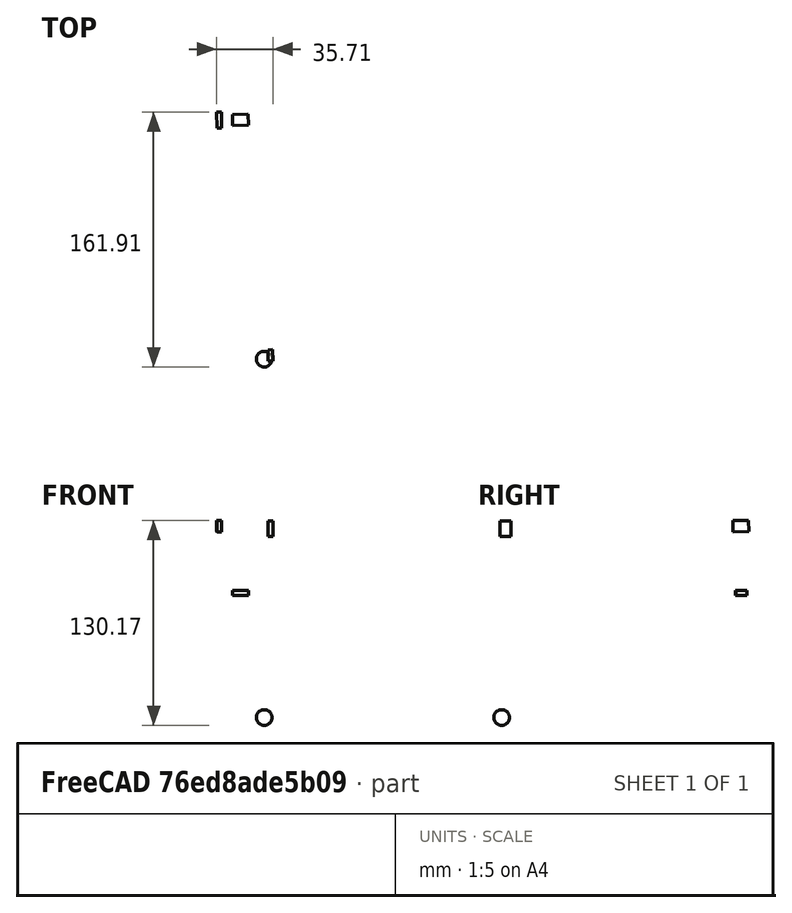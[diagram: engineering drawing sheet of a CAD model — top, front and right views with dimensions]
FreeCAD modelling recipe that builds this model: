
FCSTD DOCUMENT  (FreeCAD 2024.2R36189 (Git))
Label: 3axis_robot_forced_reduced
License: All rights reserved
LicenseURL: https://en.wikipedia.org/wiki/All_rights_reserved
objects: App::FeaturePython×9, App::Link×4, Part::FeaturePython×3, Part::Sphere×2, Assembly::JointGroup×1, Assembly::AssemblyObject×1
note: 5 computed .brp shape members not serialized (recipe doc carries the construction recipe); baked Part::Feature solids carry a one-line shape summary decoded from their .brp
EXTERNAL_REF file=base.FCStd obj=Part
EXTERNAL_REF file=arm0.FCStd obj=Part
EXTERNAL_REF file=arm1.FCStd obj=Part
EXTERNAL_REF file=arm2.FCStd obj=Part

FEATURE [App::Link] base  label="base 🔒"
  LinkedObject = -> <external base.FCStd>#Part
FEATURE [App::Link] arm0
  LinkPlacement = pos=(0,0,7) rot=(0,0,1;0.017159rad)
  LinkedObject = -> <external arm0.FCStd>#Part
  Placement = pos=(0,0,7) rot=(0,0,1;0.017159rad)
FEATURE [App::Link] arm1
  LinkPlacement = pos=(7.99882,0.137262,71) rot=(0.568594,0.584797,-0.578544;4.18519rad)
  LinkedObject = -> <external arm1.FCStd>#Part
  Placement = pos=(7.99882,0.137262,71) rot=(0.568594,0.584797,-0.578544;4.18519rad)
FEATURE [App::Link] arm2
  LinkPlacement = pos=(17.5713,-149.712,69.3598) rot=(0.707165,-0.000774,-0.707048;3.11578rad)
  LinkedObject = -> <external arm2.FCStd>#Part
  Placement = pos=(17.5713,-149.712,69.3598) rot=(0.707165,-0.000774,-0.707048;3.11578rad)
FEATURE [App::FeaturePython] GroundedJoint  # Assembly grounded joint (typed FeaturePython)
  ObjectToGround = -> base
FEATURE [App::FeaturePython] Revolute  # Assembly joint (typed FeaturePython)
  Activated = true
  Detach1 = false
  Detach2 = false
  Distance = 0
  Element1 = Edge30
  Element2 = Edge3
  JointType = 1 (Revolute)
  Object1 = Body
  Object2 = Body
  Offset = (0,0,-3)
  Part1 = -> base
  Part2 = -> arm0
  Placement1 = pos=(0,0,4) rot=(0,0,1;0rad)
  Placement2 = pos=(0,0,-3) rot=(0,0,1;0rad)
  Rotation = 0
  Vertex1 = Edge30
  Vertex2 = Edge3
FEATURE [App::FeaturePython] Revolute001  # Assembly joint (typed FeaturePython)
  Activated = true
  Detach1 = false
  Detach2 = false
  Distance = 0
  Element1 = Edge18
  Element2 = Edge23
  JointType = 1 (Revolute)
  Object1 = Body001
  Object2 = Body
  Offset = (0,0,-3)
  Part1 = -> arm1
  Part2 = -> arm0
  Placement2 = pos=(8,5.2e-15,64) rot=(0.57735,0.57735,0.57735;2.0944rad)
  Rotation = 0
  Vertex1 = Edge18
  Vertex2 = Edge23
FEATURE [App::FeaturePython] Revolute002  # Assembly joint (typed FeaturePython)
  Activated = true
  Detach1 = false
  Detach2 = false
  Distance = 0
  Element1 = Edge4
  Element2 = Edge17
  JointType = 1 (Revolute)
  Object1 = Body
  Object2 = Body001
  Offset = (0,0,2)
  Part1 = -> arm2
  Part2 = -> arm1
  Placement1 = pos=(0,0,5) rot=(0,0,1;0rad)
  Placement2 = pos=(-150,-4.1e-15,-2) rot=(1,0,0;3.14159rad)
  Rotation = 0
  Vertex1 = Edge4
  Vertex2 = Edge17
FEATURE [Part::FeaturePython] MotorObserver0  # WARN: FeaturePython — macro-defined, semantics opaque (R4)
  Enabled = true
  Placement = pos=(0,0,28.5) rot=(0,0,1;0.017159rad)
  TransfAngle = 0.983114
FEATURE [Part::FeaturePython] MotorObserver1  # WARN: FeaturePython — macro-defined, semantics opaque (R4)
  Enabled = true
  Placement = pos=(-13.498,-0.231629,71) rot=(0.568594,0.584797,-0.578544;4.18519rad)
  SupportObject = -> arm0
  TransfAngle = 359.373
FEATURE [Part::FeaturePython] MotorObserver2  # WARN: FeaturePython — macro-defined, semantics opaque (R4)
  Enabled = true
  Placement = pos=(19.0711,-149.686,69.3598) rot=(-0.018251,0.999833,-0.001094;1.5708rad)
  SupportObject = -> arm1
  TransfAngle = 0.0173308
FEATURE [App::FeaturePython] Fixed  # Assembly joint (typed FeaturePython)
  Activated = true
  Detach1 = false
  Detach2 = false
  Distance = 0
  Element1 = Face5
  Element2 = Edge4
  JointType = 0 (Fixed)
  Object1 = MotorObserver0
  Object2 = Body
  Offset = (0,0,0)
  Part1 = -> MotorObserver0
  Part2 = -> arm0
  Placement1 = pos=(1e-16,0,-1.5) rot=(0,0,1;0rad)
  Placement2 = pos=(0,0,20) rot=(0,0,1;0rad)
  Rotation = 0
  Vertex1 = Face5
  Vertex2 = Edge4
FEATURE [App::FeaturePython] Fixed001  # Assembly joint (typed FeaturePython)
  Activated = true
  Detach1 = false
  Detach2 = false
  Distance = 0
  Element1 = Face5
  Element2 = Edge47
  JointType = 0 (Fixed)
  Object1 = MotorObserver1
  Object2 = Body001
  Offset = (0,0,0)
  Part1 = -> MotorObserver1
  Part2 = -> arm1
  Placement1 = pos=(0,0,-1.5) rot=(0,0,1;0rad)
  Placement2 = pos=(0,0,20) rot=(0,0,1;0rad)
  Rotation = 0
  Vertex1 = Face5
  Vertex2 = Edge47
FEATURE [App::FeaturePython] Revolute003  label="Fixed002"  # Assembly joint (typed FeaturePython)
  Activated = true
  Detach1 = false
  Detach2 = false
  Distance = 0
  Element1 = Face5
  Element2 = Edge3
  JointType = 0 (Fixed)
  Object1 = MotorObserver2
  Object2 = Body
  Offset = (0,0,0)
  Part1 = -> MotorObserver2
  Part2 = -> arm2
  Placement1 = pos=(0,-2.84e-14,-1.5) rot=(0,0,1;0rad)
  Rotation = 0
  Vertex1 = Face5
  Vertex2 = Edge3
FEATURE [Part::Sphere] Sphere  label="ForcedSphere 🔒"
  Angle1 = -90
  Angle2 = 90
  Angle3 = 360
  AttacherType = Attacher::AttachEngine3D
  Placement = pos=(15.1115,-152.076,-50.6177) rot=(-0.015289,0.999766,-0.015289;1.57103rad)
  Radius = 5
FEATURE [Part::Sphere] Sphere001  label="ForcingSphere"
  Angle1 = -90
  Angle2 = 90
  Angle3 = 360
  AttacherType = Attacher::AttachEngine3D
  Placement = pos=(15.1115,-152.076,-50.6177) rot=(0,0,1;0rad)
  Radius = 5
FEATURE [App::FeaturePython] Ball  # Assembly joint (typed FeaturePython)
  Activated = true
  Detach1 = false
  Detach2 = false
  Distance = 0
  Element1 = Face1
  Element2 = Edge8
  JointType = 4 (Ball)
  Object1 = Sphere
  Object2 = Body
  Offset = (0,0,0)
  Part1 = -> Sphere
  Part2 = -> arm2
  Placement2 = pos=(120,0,2.5) rot=(0,0,1;0rad)
  Rotation = 0
  Vertex1 = Face1
  Vertex2 = Edge8
FEATURE [App::FeaturePython] GroundedJoint001  label="GroundedSphereJoint"  # Assembly grounded joint (typed FeaturePython)
  ObjectToGround = -> Sphere
  Placement = pos=(15.1115,-152.076,-50.6177) rot=(-0.015289,0.999766,-0.015289;1.57103rad)
FEATURE [Assembly::JointGroup] Joints
  Group = -> [GroundedJoint,Revolute,Revolute001,Revolute002,Fixed,Fixed001,Revolute003,Ball,GroundedJoint001]
FEATURE [Assembly::AssemblyObject] Assembly  label="3axis_robot"
  Group = -> [Joints,base,arm0,arm1,arm2,GroundedJoint,Revolute,Revolute001,Revolute002,MotorObserver0,MotorObserver1,MotorObserver2,Fixed,Fixed001,Revolute003,Sphere,Sphere001,Ball,GroundedJoint001]
  Origin = -> Origin
  Type = Assembly

RESOLVED EXTERNAL PARTS (link-assembly join: the EXTERNAL_REF files above that resolve inside this repo's crawl, each included once):
---- part arm0.FCStd = doc fcstd_d5e03bab67c2 ----
FCSTD DOCUMENT  (FreeCAD 2024.1R35694 (Git))
Label: arm0
License: All rights reserved
LicenseURL: https://en.wikipedia.org/wiki/All_rights_reserved
objects: Sketcher::SketchObject×11, PartDesign::Pad×6, PartDesign::Hole×3, PartDesign::Body×2, PartDesign::Pocket×2, PartDesign::Fillet×1, App::Part×1
note: 37 computed .brp shape members not serialized (recipe doc carries the construction recipe); baked Part::Feature solids carry a one-line shape summary decoded from their .brp

FEATURE [Sketcher::SketchObject] Sketch
  FullyConstrained = true
  MapMode = 5
  Support = -> [XY_Plane001]
  sketch-geometry (5):
    g0: Circle CenterX=0 CenterY=0 CenterZ=0 NormalX=0 NormalY=0 NormalZ=1 AngleXU=0 Radius=2.5
    g1: ArcOfCircle CenterX=0 CenterY=0 CenterZ=0 NormalX=0 NormalY=0 NormalZ=1 AngleXU=0 Radius=7.5 StartAngle=1.5708 EndAngle=4.71239
    g2: LineSegment StartX=-1.2e-15 StartY=7.5 StartZ=0 EndX=15 EndY=7.5 EndZ=0
    g3: LineSegment StartX=15 StartY=7.5 StartZ=0 EndX=15 EndY=-7.5 EndZ=0
    g4: LineSegment StartX=15 StartY=-7.5 StartZ=0 EndX=1.8e-15 EndY=-7.5 EndZ=0
  constraints (12):
    c: Coincident(g0,g-1)
    c: Coincident(g1,g0)
    c: Diameter(g0) = 5
    c: Diameter(g1) = 15
    c: Horizontal(g2)
    c: Coincident(g2,g3)
    c: Vertical(g3)
    c: Coincident(g3,g4)
    c: Horizontal(g4)
    c: Tangent(g1,g4) = 1.5708
    c: Tangent(g1,g2) = 1.5708
    c: DistanceX(g2,g2) = 15
FEATURE [PartDesign::Pad] Pad
  Direction = (0,0,1)
  Length = 20
  Length2 = 10
  Profile = -> Sketch
  ReferenceAxis = -> Sketch [N_Axis]
  Refine = true
  Type = 0
FEATURE [Sketcher::SketchObject] Sketch001
  ExternalGeometry = -> [Pad]
  FullyConstrained = true
  MapMode = 5
  Placement = pos=(15,0,0) rot=(0.57735,0.57735,0.57735;2.0944rad)
  Support = -> [Pad]
  sketch-geometry (8):
    g0: LineSegment StartX=-7.5 StartY=0 StartZ=0 EndX=-21 EndY=43 EndZ=0
    g1: LineSegment StartX=-21 StartY=43 StartZ=0 EndX=-21 EndY=85 EndZ=0
    g2: LineSegment StartX=-21 StartY=85 StartZ=0 EndX=21 EndY=85 EndZ=0
    g3: LineSegment StartX=21 StartY=85 StartZ=0 EndX=21 EndY=43 EndZ=0
    g4: LineSegment StartX=21 StartY=43 StartZ=0 EndX=7.5 EndY=0 EndZ=0
    g5: LineSegment StartX=7.5 StartY=0 StartZ=0 EndX=-7.5 EndY=0 EndZ=0
    g6: GeomPoint X=5.2e-15 Y=64 Z=0
    g7: Circle CenterX=5.2e-15 CenterY=64 CenterZ=0 NormalX=0 NormalY=0 NormalZ=1 AngleXU=0 Radius=11.25
  constraints (18):
    c: PointOnObject(g0,g-1)
    c: Coincident(g0,g1)
    c: Vertical(g1)
    c: Coincident(g1,g2)
    c: Coincident(g2,g3)
    c: Coincident(g3,g4)
    c: Coincident(g4,g5)
    c: Coincident(g5,g0)
    c: Symmetric(g0,g3,g-2)
    c: Symmetric(g1,g2,g-2)
    c: DistanceX(g2,g2) = 42
    c: DistanceY(g3,g3) = 42
    c: Symmetric(g0,g4,g-2)
    c: DistanceX(g5,g5) = 15
    c: Symmetric(g1,g3,g6)
    c: Coincident(g7,g6)
    c: Diameter(g7) = 22.5
    c: DistanceY(g-1,g3) = 43
FEATURE [PartDesign::Pad] Pad001
  BaseFeature = -> Pad
  Direction = (1,0,0)
  Length = 4
  Length2 = 10
  Profile = -> Sketch001
  ReferenceAxis = -> Sketch001 [N_Axis]
  Refine = true
  Reversed = true
  Type = 0
FEATURE [Sketcher::SketchObject] Sketch003
  ExternalGeometry = -> [Pad001]
  FullyConstrained = true
  MapMode = 5
  Placement = pos=(11,0,0) rot=(0.57735,-0.57735,-0.57735;2.0944rad)
  Support = -> [Pad001]
  sketch-geometry (5):
    g0: Circle CenterX=15.5 CenterY=79.5 CenterZ=0 NormalX=0 NormalY=0 NormalZ=1 AngleXU=0 Radius=1.5
    g1: LineSegment StartX=-5.2e-15 StartY=64 StartZ=0 EndX=11.25 EndY=64 EndZ=0
    g2: Circle CenterX=-15.5 CenterY=79.5 CenterZ=0 NormalX=0 NormalY=0 NormalZ=1 AngleXU=0 Radius=1.5
    g3: Circle CenterX=15.5 CenterY=48.5 CenterZ=0 NormalX=0 NormalY=0 NormalZ=1 AngleXU=0 Radius=1.5
    g4: Circle CenterX=-15.5 CenterY=48.5 CenterZ=0 NormalX=0 NormalY=0 NormalZ=1 AngleXU=0 Radius=1.5
  constraints (12):
    c: DistanceY(g-3,g0) = 15.5
    c: DistanceX(g-3,g0) = 15.5
    c: Diameter(g0) = 3
    c: Coincident(g1,g-3)
    c: Horizontal(g1)
    c: PointOnObject(g1,g-3)
    c: Diameter(g2) = 3
    c: Diameter(g3) = 3
    c: Diameter(g4) = 3
    c: Symmetric(g2,g0,g-2)
    c: Symmetric(g4,g3,g-2)
    c: Symmetric(g3,g0,g1)
FEATURE [PartDesign::Hole] Hole
  BaseFeature = -> Pad001
  CustomThreadClearance = 0
  Depth = 25
  DepthType = 0
  Diameter = 3.4
  DrillForDepth = false
  DrillPoint = 1
  DrillPointAngle = 118
  HoleCutCountersinkAngle = 90
  HoleCutCustomValues = false
  HoleCutDepth = 2
  HoleCutDiameter = 6.1
  HoleCutType = 1
  ModelThread = false
  Profile = -> Sketch003
  Refine = true
  Tapered = false
  TaperedAngle = 90
  ThreadClass = 0
  ThreadDepth = 25
  ThreadDepthType = 0
  ThreadDirection = 0
  ThreadFit = 0
  ThreadSize = 9
  ThreadType = 1
  Threaded = false
  UseCustomThreadClearance = false
FEATURE [Sketcher::SketchObject] Sketch004
  ExternalGeometry = -> [Hole]
  FullyConstrained = true
  MapMode = 5
  Placement = pos=(0,0,20) rot=(0,0,1;0rad)
  Support = -> [Hole]
  sketch-geometry (1):
    g0: Circle CenterX=0 CenterY=0 CenterZ=0 NormalX=0 NormalY=0 NormalZ=1 AngleXU=0 Radius=2.5
  constraints (2):
    c: Coincident(g0,g-3)
    c: Equal(g0,g-3)
FEATURE [PartDesign::Pad] Pad002
  BaseFeature = -> Hole
  Direction = (0,0,1)
  Length = 2
  Length2 = 10
  Profile = -> Sketch004
  ReferenceAxis = -> Sketch004 [N_Axis]
  Refine = true
  Reversed = true
  Type = 0
FEATURE [PartDesign::Body] Body  label="arm0-skel"
  Group = -> [Sketch,Pad,Sketch001,Pad001,Sketch003,Hole,Sketch004,Pad002]
  Origin = -> Origin001
  Tip = -> Pad002
FEATURE [Sketcher::SketchObject] Sketch008
  FullyConstrained = true
  MapMode = 5
  Support = -> [XY_Plane002]
  sketch-geometry (5):
    g0: Circle CenterX=0 CenterY=0 CenterZ=0 NormalX=0 NormalY=0 NormalZ=1 AngleXU=0 Radius=2.5
    g1: ArcOfCircle CenterX=0 CenterY=0 CenterZ=0 NormalX=0 NormalY=0 NormalZ=1 AngleXU=0 Radius=7.5 StartAngle=1.5708 EndAngle=4.71239
    g2: LineSegment StartX=-1.2e-15 StartY=7.5 StartZ=0 EndX=15 EndY=7.5 EndZ=0
    g3: LineSegment StartX=15 StartY=7.5 StartZ=0 EndX=15 EndY=-7.5 EndZ=0
    g4: LineSegment StartX=15 StartY=-7.5 StartZ=0 EndX=1.8e-15 EndY=-7.5 EndZ=0
  constraints (12):
    c: Coincident(g0,g-1)
    c: Coincident(g1,g0)
    c: Diameter(g0) = 5
    c: Diameter(g1) = 15
    c: Horizontal(g2)
    c: Coincident(g2,g3)
    c: Vertical(g3)
    c: Coincident(g3,g4)
    c: Horizontal(g4)
    c: Tangent(g1,g4) = 1.5708
    c: Tangent(g1,g2) = 1.5708
    c: DistanceX(g2,g2) = 15
FEATURE [PartDesign::Pad] Pad003
  Direction = (0,0,1)
  Length = 20
  Length2 = 10
  Profile = -> Sketch008
  ReferenceAxis = -> Sketch008 [N_Axis]
  Refine = true
  Type = 0
FEATURE [Sketcher::SketchObject] Sketch009
  ExternalGeometry = -> [Pad003]
  FullyConstrained = true
  MapMode = 5
  Placement = pos=(15,0,0) rot=(0.57735,0.57735,0.57735;2.0944rad)
  Support = -> [Pad003]
  sketch-geometry (8):
    g0: LineSegment StartX=-7.5 StartY=0 StartZ=0 EndX=-21 EndY=43 EndZ=0
    g1: LineSegment StartX=-21 StartY=43 StartZ=0 EndX=-21 EndY=85 EndZ=0
    g2: LineSegment StartX=-21 StartY=85 StartZ=0 EndX=21 EndY=85 EndZ=0
    g3: LineSegment StartX=21 StartY=85 StartZ=0 EndX=21 EndY=43 EndZ=0
    g4: LineSegment StartX=21 StartY=43 StartZ=0 EndX=7.5 EndY=0 EndZ=0
    g5: LineSegment StartX=7.5 StartY=0 StartZ=0 EndX=-7.5 EndY=0 EndZ=0
    g6: GeomPoint X=4.8e-15 Y=64 Z=0
    g7: Circle CenterX=4.8e-15 CenterY=64 CenterZ=0 NormalX=0 NormalY=0 NormalZ=1 AngleXU=0 Radius=11.25
  constraints (18):
    c: PointOnObject(g0,g-1)
    c: Coincident(g0,g1)
    c: Vertical(g1)
    c: Coincident(g1,g2)
    c: Coincident(g2,g3)
    c: Coincident(g3,g4)
    c: Coincident(g4,g5)
    c: Coincident(g5,g0)
    c: Symmetric(g0,g3,g-2)
    c: Symmetric(g1,g2,g-2)
    c: DistanceX(g2,g2) = 42
    c: DistanceY(g3,g3) = 42
    c: Symmetric(g0,g4,g-2)
    c: DistanceX(g5,g5) = 15
    c: Symmetric(g1,g3,g6)
    c: Coincident(g7,g6)
    c: Diameter(g7) = 22.5
    c: DistanceY(g-1,g3) = 43
FEATURE [PartDesign::Pad] Pad004
  BaseFeature = -> Pad003
  Direction = (1,0,0)
  Length = 4
  Length2 = 10
  Profile = -> Sketch009
  ReferenceAxis = -> Sketch009 [N_Axis]
  Refine = true
  Reversed = true
  Type = 0
FEATURE [Sketcher::SketchObject] Sketch010
  ExternalGeometry = -> [Pad004]
  FullyConstrained = true
  MapMode = 5
  Placement = pos=(11,0,0) rot=(0.57735,-0.57735,-0.57735;2.0944rad)
  Support = -> [Pad004]
  sketch-geometry (5):
    g0: Circle CenterX=15.5 CenterY=79.5 CenterZ=0 NormalX=0 NormalY=0 NormalZ=1 AngleXU=0 Radius=1.5
    g1: LineSegment StartX=-4.8e-15 StartY=64 StartZ=0 EndX=11.25 EndY=64 EndZ=0
    g2: Circle CenterX=-15.5 CenterY=79.5 CenterZ=0 NormalX=0 NormalY=0 NormalZ=1 AngleXU=0 Radius=1.5
    g3: Circle CenterX=15.5 CenterY=48.5 CenterZ=0 NormalX=0 NormalY=0 NormalZ=1 AngleXU=0 Radius=1.5
    g4: Circle CenterX=-15.5 CenterY=48.5 CenterZ=0 NormalX=0 NormalY=0 NormalZ=1 AngleXU=0 Radius=1.5
  constraints (12):
    c: DistanceY(g-3,g0) = 15.5
    c: DistanceX(g-3,g0) = 15.5
    c: Diameter(g0) = 3
    c: Coincident(g1,g-3)
    c: Horizontal(g1)
    c: PointOnObject(g1,g-3)
    c: Diameter(g2) = 3
    c: Diameter(g3) = 3
    c: Diameter(g4) = 3
    c: Symmetric(g2,g0,g-2)
    c: Symmetric(g4,g3,g-2)
    c: Symmetric(g3,g0,g1)
FEATURE [PartDesign::Hole] Hole002
  BaseFeature = -> Pad004
  CustomThreadClearance = 0
  Depth = 25
  DepthType = 0
  Diameter = 3.4
  DrillForDepth = false
  DrillPoint = 1
  DrillPointAngle = 118
  HoleCutCountersinkAngle = 90
  HoleCutCustomValues = false
  HoleCutDepth = 2
  HoleCutDiameter = 6.1
  HoleCutType = 1
  ModelThread = false
  Profile = -> Sketch010
  Refine = true
  Tapered = false
  TaperedAngle = 90
  ThreadClass = 0
  ThreadDepth = 25
  ThreadDepthType = 0
  ThreadDirection = 0
  ThreadFit = 0
  ThreadSize = 9
  ThreadType = 1
  Threaded = false
  UseCustomThreadClearance = false
FEATURE [Sketcher::SketchObject] Sketch011
  ExternalGeometry = -> [Hole002]
  FullyConstrained = true
  MapMode = 5
  Placement = pos=(0,0,20) rot=(0,0,1;0rad)
  Support = -> [Hole002]
  sketch-geometry (1):
    g0: Circle CenterX=0 CenterY=0 CenterZ=0 NormalX=0 NormalY=0 NormalZ=1 AngleXU=0 Radius=2.5
  constraints (2):
    c: Coincident(g0,g-3)
    c: Equal(g0,g-3)
FEATURE [PartDesign::Pad] Pad005
  BaseFeature = -> Hole002
  Direction = (0,0,1)
  Length = 2
  Length2 = 10
  Profile = -> Sketch011
  ReferenceAxis = -> Sketch011 [N_Axis]
  Refine = true
  Reversed = true
  Type = 0
FEATURE [Sketcher::SketchObject] Sketch012
  FullyConstrained = true
  MapMode = 5
  Placement = pos=(0,0,0) rot=(1,0,0;3.14159rad)
  Support = -> [Pad005]
  sketch-geometry (4):
    g0: LineSegment StartX=0 StartY=1 StartZ=0 EndX=0 EndY=-1 EndZ=0
    g1: LineSegment StartX=0 StartY=-1 StartZ=0 EndX=10 EndY=-1 EndZ=0
    g2: LineSegment StartX=10 StartY=-1 StartZ=0 EndX=10 EndY=1 EndZ=0
    g3: LineSegment StartX=10 StartY=1 StartZ=0 EndX=0 EndY=1 EndZ=0
  constraints (11):
    c: Coincident(g0,g1)
    c: Coincident(g1,g2)
    c: Coincident(g2,g3)
    c: Coincident(g3,g0)
    c: Vertical(g0)
    c: Horizontal(g1)
    c: Horizontal(g3)
    c: PointOnObject(g0,g-2)
    c: Symmetric(g1,g2,g-1)
    c: DistanceY(g2,g2) = 2
    c: DistanceX(g3,g3) = 10
FEATURE [PartDesign::Pocket] Pocket002
  BaseFeature = -> Pad005
  Direction = (0,0,1)
  Length = 5
  Length2 = 5
  Profile = -> Sketch012
  ReferenceAxis = -> Sketch012 [N_Axis]
  Refine = true
  Type = 1
FEATURE [Sketcher::SketchObject] Sketch013
  FullyConstrained = true
  MapMode = 5
  Placement = pos=(0,-7.5,0) rot=(1,0,0;1.5708rad)
  Support = -> [Pocket002]
  sketch-geometry (1):
    g0: Circle CenterX=6 CenterY=10 CenterZ=0 NormalX=0 NormalY=0 NormalZ=1 AngleXU=0 Radius=1.5
  constraints (3):
    c: DistanceY(g-1,g0) = 10
    c: DistanceX(g-1,g0) = 6
    c: Diameter(g0) = 3
FEATURE [PartDesign::Hole] Hole003
  BaseFeature = -> Pocket002
  CustomThreadClearance = 0
  Depth = 25
  DepthType = 0
  Diameter = 4.5
  DrillForDepth = false
  DrillPoint = 1
  DrillPointAngle = 118
  HoleCutCountersinkAngle = 90
  HoleCutCustomValues = false
  HoleCutDepth = 0
  HoleCutDiameter = 6.1
  HoleCutType = 0
  ModelThread = false
  Profile = -> Sketch013
  Refine = true
  Tapered = false
  TaperedAngle = 90
  ThreadClass = 0
  ThreadDepth = 25
  ThreadDepthType = 0
  ThreadDirection = 0
  ThreadFit = 0
  ThreadSize = 11
  ThreadType = 1
  Threaded = false
  UseCustomThreadClearance = false
FEATURE [Sketcher::SketchObject] Sketch014
  ExternalGeometry = -> [Hole003]
  FullyConstrained = true
  MapMode = 5
  Placement = pos=(0,7.5,0) rot=(0,0.707107,0.707107;3.14159rad)
  Support = -> [Hole003]
  sketch-geometry (7):
    g0: LineSegment StartX=-1.95855 StartY=10 StartZ=0 EndX=-3.97927 EndY=13.5 EndZ=0
    g1: LineSegment StartX=-3.97927 StartY=13.5 StartZ=0 EndX=-8.02073 EndY=13.5 EndZ=0
    g2: LineSegment StartX=-8.02073 StartY=13.5 StartZ=0 EndX=-10.0415 EndY=10 EndZ=0
    g3: LineSegment StartX=-10.0415 StartY=10 StartZ=0 EndX=-8.02073 EndY=6.5 EndZ=0
    g4: LineSegment StartX=-8.02073 StartY=6.5 StartZ=0 EndX=-3.97927 EndY=6.5 EndZ=0
    g5: LineSegment StartX=-3.97927 StartY=6.5 StartZ=0 EndX=-1.95855 EndY=10 EndZ=0
    g6: Circle CenterX=-6 CenterY=10 CenterZ=0 NormalX=0 NormalY=0 NormalZ=1 AngleXU=0 Radius=4.04145
  constraints (16):
    c: Coincident(g0,g1)
    c: Coincident(g1,g2)
    c: Coincident(g2,g3)
    c: Coincident(g3,g4)
    c: Coincident(g4,g5)
    c: Coincident(g5,g0)
    c: Equal(g0, g1-g5) x5
    c: PointOnObject(g0,g6)
    c: PointOnObject(g1,g6)
    c: PointOnObject(g2,g6)
    c: PointOnObject(g3,g6)
    c: PointOnObject(g4,g6)
    c: PointOnObject(g5,g6)
    c: Coincident(g6,g-3)
    c: Horizontal(g1)
    c: DistanceY(g4,g0) = 7
FEATURE [PartDesign::Pocket] Pocket003
  BaseFeature = -> Hole003
  Direction = (0,-1,2e-16)
  Length = 4
  Length2 = 5
  Profile = -> Sketch014
  ReferenceAxis = -> Sketch014 [N_Axis]
  Refine = true
  Type = 0
FEATURE [PartDesign::Fillet] Fillet
  Base = -> Pocket003 [Edge77,Edge78,Edge65,Edge54]
  BaseFeature = -> Pocket003
  Radius = 6
  Refine = true
  SupportTransform = false
  UseAllEdges = false
FEATURE [PartDesign::Body] Body001  label="arm0s"
  Group = -> [Sketch008,Pad003,Sketch009,Pad004,Sketch010,Hole002,Sketch011,Pad005,Sketch012,Pocket002,Sketch013,Hole003,Sketch014,Pocket003,Fillet]
  Origin = -> Origin002
  Tip = -> Fillet
FEATURE [App::Part] Part  label="arm0"
  Group = -> [Body,Body001]
  Origin = -> Origin
---- part arm1.FCStd = doc fcstd_95fd860c3653 ----
FCSTD DOCUMENT  (FreeCAD 2024.1R35694 (Git))
Label: arm1
License: All rights reserved
LicenseURL: https://en.wikipedia.org/wiki/All_rights_reserved
objects: Sketcher::SketchObject×17, PartDesign::Pad×11, PartDesign::Chamfer×8, PartDesign::Plane×4, PartDesign::Hole×3, PartDesign::Pocket×3, PartDesign::Body×2, PartDesign::Fillet×1, App::Part×1
note: 75 computed .brp shape members not serialized (recipe doc carries the construction recipe); baked Part::Feature solids carry a one-line shape summary decoded from their .brp

FEATURE [Sketcher::SketchObject] Sketch
  FullyConstrained = true
  MapMode = 5
  Support = -> [XY_Plane001]
  sketch-geometry (5):
    g0: Circle CenterX=0 CenterY=0 CenterZ=0 NormalX=0 NormalY=0 NormalZ=1 AngleXU=0 Radius=2.5
    g1: ArcOfCircle CenterX=0 CenterY=0 CenterZ=0 NormalX=0 NormalY=0 NormalZ=1 AngleXU=0 Radius=7.5 StartAngle=1.5708 EndAngle=4.71239
    g2: LineSegment StartX=-1.2e-15 StartY=7.5 StartZ=0 EndX=15 EndY=7.5 EndZ=0
    g3: LineSegment StartX=15 StartY=7.5 StartZ=0 EndX=15 EndY=-7.5 EndZ=0
    g4: LineSegment StartX=15 StartY=-7.5 StartZ=0 EndX=1.8e-15 EndY=-7.5 EndZ=0
  constraints (12):
    c: Coincident(g0,g-1)
    c: Coincident(g1,g0)
    c: Diameter(g0) = 5
    c: Diameter(g1) = 15
    c: Horizontal(g2)
    c: Coincident(g2,g3)
    c: Vertical(g3)
    c: Coincident(g3,g4)
    c: Horizontal(g4)
    c: Tangent(g1,g4) = 1.5708
    c: Tangent(g1,g2) = 1.5708
    c: DistanceX(g2,g2) = 15
FEATURE [PartDesign::Pad] Pad
  Direction = (0,0,1)
  Length = 20
  Length2 = 10
  Profile = -> Sketch
  ReferenceAxis = -> Sketch [N_Axis]
  Refine = true
  Type = 0
FEATURE [Sketcher::SketchObject] Sketch001
  ExternalGeometry = -> [Pad]
  FullyConstrained = true
  MapMode = 5
  Placement = pos=(15,0,0) rot=(0.57735,0.57735,0.57735;2.0944rad)
  Support = -> [Pad]
  sketch-geometry (8):
    g0: LineSegment StartX=-7.5 StartY=0 StartZ=0 EndX=-21 EndY=11 EndZ=0
    g1: LineSegment StartX=-21 StartY=11 StartZ=0 EndX=-21 EndY=53 EndZ=0
    g2: LineSegment StartX=-21 StartY=53 StartZ=0 EndX=21 EndY=53 EndZ=0
    g3: LineSegment StartX=21 StartY=53 StartZ=0 EndX=21 EndY=11 EndZ=0
    g4: LineSegment StartX=21 StartY=11 StartZ=0 EndX=7.5 EndY=0 EndZ=0
    g5: LineSegment StartX=7.5 StartY=0 StartZ=0 EndX=-7.5 EndY=0 EndZ=0
    g6: GeomPoint X=-1.2e-15 Y=32 Z=0
    g7: Circle CenterX=-1.2e-15 CenterY=32 CenterZ=0 NormalX=0 NormalY=0 NormalZ=1 AngleXU=0 Radius=11.25
  constraints (18):
    c: PointOnObject(g0,g-1)
    c: Coincident(g0,g1)
    c: Vertical(g1)
    c: Coincident(g1,g2)
    c: Coincident(g2,g3)
    c: Coincident(g3,g4)
    c: Coincident(g4,g5)
    c: Coincident(g5,g0)
    c: Symmetric(g0,g3,g-2)
    c: Symmetric(g1,g2,g-2)
    c: DistanceX(g2,g2) = 42
    c: DistanceY(g3,g3) = 42
    c: Symmetric(g0,g4,g-2)
    c: DistanceX(g5,g5) = 15
    c: Symmetric(g1,g3,g6)
    c: Coincident(g7,g6)
    c: Diameter(g7) = 22.5
    c: DistanceY(g-1,g3) = 11
FEATURE [PartDesign::Pad] Pad001
  BaseFeature = -> Pad
  Direction = (1,0,0)
  Length = 4
  Length2 = 10
  Profile = -> Sketch001
  ReferenceAxis = -> Sketch001 [N_Axis]
  Refine = true
  Reversed = true
  Type = 0
FEATURE [Sketcher::SketchObject] Sketch003
  ExternalGeometry = -> [Pad001]
  FullyConstrained = true
  MapMode = 5
  Placement = pos=(11,0,0) rot=(0.57735,-0.57735,-0.57735;2.0944rad)
  Support = -> [Pad001]
  sketch-geometry (5):
    g0: Circle CenterX=15.5 CenterY=47.5 CenterZ=0 NormalX=0 NormalY=0 NormalZ=1 AngleXU=0 Radius=1.5
    g1: LineSegment StartX=1.2e-15 StartY=32 StartZ=0 EndX=11.25 EndY=32 EndZ=0
    g2: Circle CenterX=-15.5 CenterY=47.5 CenterZ=0 NormalX=0 NormalY=0 NormalZ=1 AngleXU=0 Radius=1.5
    g3: Circle CenterX=15.5 CenterY=16.5 CenterZ=0 NormalX=0 NormalY=0 NormalZ=1 AngleXU=0 Radius=1.5
    g4: Circle CenterX=-15.5 CenterY=16.5 CenterZ=0 NormalX=0 NormalY=0 NormalZ=1 AngleXU=0 Radius=1.5
  constraints (12):
    c: DistanceY(g-3,g0) = 15.5
    c: DistanceX(g-3,g0) = 15.5
    c: Diameter(g0) = 3
    c: Coincident(g1,g-3)
    c: Horizontal(g1)
    c: PointOnObject(g1,g-3)
    c: Diameter(g2) = 3
    c: Diameter(g3) = 3
    c: Diameter(g4) = 3
    c: Symmetric(g2,g0,g-2)
    c: Symmetric(g4,g3,g-2)
    c: Symmetric(g3,g0,g1)
FEATURE [PartDesign::Hole] Hole
  BaseFeature = -> Pad001
  CustomThreadClearance = 0
  Depth = 25
  DepthType = 0
  Diameter = 3.4
  DrillForDepth = false
  DrillPoint = 1
  DrillPointAngle = 118
  HoleCutCountersinkAngle = 90
  HoleCutCustomValues = false
  HoleCutDepth = 2
  HoleCutDiameter = 6.1
  HoleCutType = 1
  ModelThread = false
  Profile = -> Sketch003
  Refine = true
  Tapered = false
  TaperedAngle = 90
  ThreadClass = 0
  ThreadDepth = 25
  ThreadDepthType = 0
  ThreadDirection = 0
  ThreadFit = 0
  ThreadSize = 9
  ThreadType = 1
  Threaded = false
  UseCustomThreadClearance = false
FEATURE [Sketcher::SketchObject] Sketch004
  ExternalGeometry = -> [Hole]
  FullyConstrained = true
  MapMode = 5
  Placement = pos=(0,0,20) rot=(0,0,1;0rad)
  Support = -> [Hole]
  sketch-geometry (1):
    g0: Circle CenterX=0 CenterY=0 CenterZ=0 NormalX=0 NormalY=0 NormalZ=1 AngleXU=0 Radius=2.5
  constraints (2):
    c: Coincident(g0,g-3)
    c: Equal(g0,g-3)
FEATURE [PartDesign::Pad] Pad002
  BaseFeature = -> Hole
  Direction = (0,0,1)
  Length = 2
  Length2 = 10
  Profile = -> Sketch004
  ReferenceAxis = -> Sketch004 [N_Axis]
  Refine = true
  Reversed = true
  Type = 0
FEATURE [Sketcher::SketchObject] Sketch005
  FullyConstrained = true
  MapMode = 5
  Placement = pos=(0,0,0) rot=(1,0,0;3.14159rad)
  Support = -> [Pad002]
  sketch-geometry (4):
    g0: LineSegment StartX=0 StartY=1 StartZ=0 EndX=0 EndY=-1 EndZ=0
    g1: LineSegment StartX=0 StartY=-1 StartZ=0 EndX=10 EndY=-1 EndZ=0
    g2: LineSegment StartX=10 StartY=-1 StartZ=0 EndX=10 EndY=1 EndZ=0
    g3: LineSegment StartX=10 StartY=1 StartZ=0 EndX=0 EndY=1 EndZ=0
  constraints (11):
    c: Coincident(g0,g1)
    c: Coincident(g1,g2)
    c: Coincident(g2,g3)
    c: Coincident(g3,g0)
    c: Vertical(g0)
    c: Horizontal(g1)
    c: Horizontal(g3)
    c: PointOnObject(g0,g-2)
    c: Symmetric(g1,g2,g-1)
    c: DistanceY(g2,g2) = 2
    c: DistanceX(g3,g3) = 10
FEATURE [PartDesign::Pocket] Pocket
  BaseFeature = -> Pad002
  Direction = (0,0,1)
  Length = 5
  Length2 = 5
  Profile = -> Sketch005
  ReferenceAxis = -> Sketch005 [N_Axis]
  Refine = true
  Type = 1
FEATURE [Sketcher::SketchObject] Sketch006
  FullyConstrained = true
  MapMode = 5
  Placement = pos=(0,-7.5,0) rot=(1,0,0;1.5708rad)
  Support = -> [Pocket]
  sketch-geometry (1):
    g0: Circle CenterX=6 CenterY=10 CenterZ=0 NormalX=0 NormalY=0 NormalZ=1 AngleXU=0 Radius=1.5
  constraints (3):
    c: DistanceY(g-1,g0) = 10
    c: DistanceX(g-1,g0) = 6
    c: Diameter(g0) = 3
FEATURE [PartDesign::Hole] Hole001
  BaseFeature = -> Pocket
  CustomThreadClearance = 0
  Depth = 25
  DepthType = 0
  Diameter = 4.5
  DrillForDepth = false
  DrillPoint = 1
  DrillPointAngle = 118
  HoleCutCountersinkAngle = 90
  HoleCutCustomValues = false
  HoleCutDepth = 0
  HoleCutDiameter = 6.1
  HoleCutType = 0
  ModelThread = false
  Profile = -> Sketch006
  Refine = true
  Tapered = false
  TaperedAngle = 90
  ThreadClass = 0
  ThreadDepth = 25
  ThreadDepthType = 0
  ThreadDirection = 0
  ThreadFit = 0
  ThreadSize = 11
  ThreadType = 1
  Threaded = false
  UseCustomThreadClearance = false
FEATURE [Sketcher::SketchObject] Sketch007
  ExternalGeometry = -> [Hole001]
  FullyConstrained = true
  MapMode = 5
  Placement = pos=(0,7.5,0) rot=(0,0.707107,0.707107;3.14159rad)
  Support = -> [Hole001]
  sketch-geometry (7):
    g0: LineSegment StartX=-6 StartY=14.0415 StartZ=0 EndX=-9.5 EndY=12.0207 EndZ=0
    g1: LineSegment StartX=-9.5 StartY=12.0207 StartZ=0 EndX=-9.5 EndY=7.97927 EndZ=0
    g2: LineSegment StartX=-9.5 StartY=7.97927 StartZ=0 EndX=-6 EndY=5.95855 EndZ=0
    g3: LineSegment StartX=-6 StartY=5.95855 StartZ=0 EndX=-2.5 EndY=7.97927 EndZ=0
    g4: LineSegment StartX=-2.5 StartY=7.97927 StartZ=0 EndX=-2.5 EndY=12.0207 EndZ=0
    g5: LineSegment StartX=-2.5 StartY=12.0207 StartZ=0 EndX=-6 EndY=14.0415 EndZ=0
    g6: Circle CenterX=-6 CenterY=10 CenterZ=0 NormalX=0 NormalY=0 NormalZ=1 AngleXU=0 Radius=4.04145
  constraints (16):
    c: Coincident(g0,g1)
    c: Coincident(g1,g2)
    c: Coincident(g2,g3)
    c: Coincident(g3,g4)
    c: Coincident(g4,g5)
    c: Coincident(g5,g0)
    c: Equal(g0, g1-g5) x5
    c: PointOnObject(g0,g6)
    c: PointOnObject(g1,g6)
    c: PointOnObject(g2,g6)
    c: PointOnObject(g3,g6)
    c: PointOnObject(g4,g6)
    c: PointOnObject(g5,g6)
    c: Coincident(g6,g-3)
    c: Vertical(g4)
    c: DistanceX(g0,g4) = 7
FEATURE [PartDesign::Pocket] Pocket001
  BaseFeature = -> Hole001
  Direction = (0,-1,2e-16)
  Length = 4
  Length2 = 5
  Profile = -> Sketch007
  ReferenceAxis = -> Sketch007 [N_Axis]
  Refine = true
  Type = 0
FEATURE [Sketcher::SketchObject] Sketch008
  ExternalGeometry = -> [Pocket001]
  FullyConstrained = true
  MapMode = 5
  Placement = pos=(0,0,0) rot=(1,0,0;3.14159rad)
  Support = -> [Pocket001]
  sketch-geometry (5):
    g0: Circle CenterX=-150 CenterY=2.37e-14 CenterZ=0 NormalX=0 NormalY=0 NormalZ=1 AngleXU=0 Radius=8
    g1: ArcOfCircle CenterX=-150 CenterY=2.37e-14 CenterZ=0 NormalX=0 NormalY=0 NormalZ=1 AngleXU=0 Radius=11 StartAngle=0.276227 EndAngle=6.00696
    g2: ArcOfCircle CenterX=0 CenterY=0 CenterZ=0 NormalX=0 NormalY=0 NormalZ=1 AngleXU=0 Radius=7.5 StartAngle=2.73008 EndAngle=3.55311
    g3: LineSegment StartX=-139.417 StartY=3 StartZ=0 EndX=-6.87386 EndY=3 EndZ=0
    g4: LineSegment StartX=-139.417 StartY=-3 StartZ=0 EndX=-6.87386 EndY=-3 EndZ=0
  constraints (14):
    c: Coincident(g1,g0)
    c: Equal(g2,g-3)
    c: Horizontal(g3)
    c: Horizontal(g4)
    c: Coincident(g1,g4)
    c: Coincident(g1,g3)
    c: Coincident(g2,g3)
    c: Coincident(g2,g4)
    c: Symmetric(g1,g1,g-1)
    c: Distance(g1,g1) = 6
    c: Diameter(g0) = 16
    c: Diameter(g1) = 22
    c: DistanceX(g0,g-1) = 150
    c: Coincident(g2,g-3)
FEATURE [PartDesign::Pad] Pad003
  BaseFeature = -> Pocket001
  Direction = (0,0,-1)
  Length = 10
  Length2 = 10
  Profile = -> Sketch008
  ReferenceAxis = -> Sketch008 [N_Axis]
  Refine = true
  Reversed = true
  Type = 0
FEATURE [PartDesign::Plane] DatumPlane
  AttachmentOffset = pos=(0,0,-145) rot=(0,0,1;0rad)
  Length = 62.49
  MapMode = 5
  Placement = pos=(-130,0,0) rot=(0.57735,0.57735,0.57735;2.0944rad)
  ResizeMode = 0
  Support = -> [Pad003]
  Width = 90.49
FEATURE [Sketcher::SketchObject] Sketch009
  ExternalGeometry = -> [Pad003]
  FullyConstrained = true
  MapMode = 5
  Placement = pos=(-130,0,0) rot=(0.57735,0.57735,0.57735;2.0944rad)
  Support = -> [DatumPlane]
  sketch-geometry (5):
    g0: Circle CenterX=-1.2e-15 CenterY=32 CenterZ=0 NormalX=0 NormalY=0 NormalZ=1 AngleXU=0 Radius=8
    g1: ArcOfCircle CenterX=-1.2e-15 CenterY=32 CenterZ=0 NormalX=0 NormalY=0 NormalZ=1 AngleXU=0 Radius=11 StartAngle=4.98862 EndAngle=10.7193
    g2: LineSegment StartX=3 StartY=10 StartZ=0 EndX=-3 EndY=10 EndZ=0
    g3: LineSegment StartX=-3 StartY=10 StartZ=0 EndX=-3 EndY=21.417 EndZ=0
    g4: LineSegment StartX=3 StartY=10 StartZ=0 EndX=3 EndY=21.417 EndZ=0
  constraints (12):
    c: Coincident(g0,g-6)
    c: Coincident(g1,g0)
    c: Diameter(g0) = 16
    c: Diameter(g1) = 22
    c: Coincident(g2,g-4)
    c: Coincident(g2,g-5)
    c: Coincident(g2,g3)
    c: Coincident(g2,g4)
    c: Vertical(g4)
    c: Vertical(g3)
    c: Coincident(g1,g3)
    c: Coincident(g1,g4)
FEATURE [PartDesign::Pad] Pad004
  BaseFeature = -> Pad003
  Direction = (1,0,0)
  Length = 5
  Length2 = 10
  Profile = -> Sketch009
  ReferenceAxis = -> Sketch009 [N_Axis]
  Refine = true
  Type = 0
FEATURE [Sketcher::SketchObject] Sketch010
  FullyConstrained = true
  MapMode = 5
  Support = -> [XY_Plane002]
  sketch-geometry (5):
    g0: Circle CenterX=0 CenterY=0 CenterZ=0 NormalX=0 NormalY=0 NormalZ=1 AngleXU=0 Radius=2.5
    g1: ArcOfCircle CenterX=0 CenterY=0 CenterZ=0 NormalX=0 NormalY=0 NormalZ=1 AngleXU=0 Radius=7.5 StartAngle=1.5708 EndAngle=4.71239
    g2: LineSegment StartX=-1.2e-15 StartY=7.5 StartZ=0 EndX=15 EndY=7.5 EndZ=0
    g3: LineSegment StartX=15 StartY=7.5 StartZ=0 EndX=15 EndY=-7.5 EndZ=0
    g4: LineSegment StartX=15 StartY=-7.5 StartZ=0 EndX=1.8e-15 EndY=-7.5 EndZ=0
  constraints (12):
    c: Coincident(g0,g-1)
    c: Coincident(g1,g0)
    c: Diameter(g0) = 5
    c: Diameter(g1) = 15
    c: Horizontal(g2)
    c: Coincident(g2,g3)
    c: Vertical(g3)
    c: Coincident(g3,g4)
    c: Horizontal(g4)
    c: Tangent(g1,g4) = 1.5708
    c: Tangent(g1,g2) = 1.5708
    c: DistanceX(g2,g2) = 15
FEATURE [PartDesign::Pad] Pad005
  Direction = (0,0,1)
  Length = 20
  Length2 = 10
  Profile = -> Sketch010
  ReferenceAxis = -> Sketch010 [N_Axis]
  Refine = true
  Type = 0
FEATURE [Sketcher::SketchObject] Sketch011
  ExternalGeometry = -> [Pad005]
  FullyConstrained = true
  MapMode = 5
  Placement = pos=(15,0,0) rot=(0.57735,0.57735,0.57735;2.0944rad)
  Support = -> [Pad005]
  sketch-geometry (8):
    g0: LineSegment StartX=-7.5 StartY=0 StartZ=0 EndX=-21 EndY=11 EndZ=0
    g1: LineSegment StartX=-21 StartY=11 StartZ=0 EndX=-21 EndY=53 EndZ=0
    g2: LineSegment StartX=-21 StartY=53 StartZ=0 EndX=21 EndY=53 EndZ=0
    g3: LineSegment StartX=21 StartY=53 StartZ=0 EndX=21 EndY=11 EndZ=0
    g4: LineSegment StartX=21 StartY=11 StartZ=0 EndX=7.5 EndY=0 EndZ=0
    g5: LineSegment StartX=7.5 StartY=0 StartZ=0 EndX=-7.5 EndY=0 EndZ=0
    g6: GeomPoint X=-1.2e-15 Y=32 Z=0
    g7: Circle CenterX=-1.2e-15 CenterY=32 CenterZ=0 NormalX=0 NormalY=0 NormalZ=1 AngleXU=0 Radius=11.25
  constraints (18):
    c: PointOnObject(g0,g-1)
    c: Coincident(g0,g1)
    c: Vertical(g1)
    c: Coincident(g1,g2)
    c: Coincident(g2,g3)
    c: Coincident(g3,g4)
    c: Coincident(g4,g5)
    c: Coincident(g5,g0)
    c: Symmetric(g0,g3,g-2)
    c: Symmetric(g1,g2,g-2)
    c: DistanceX(g2,g2) = 42
    c: DistanceY(g3,g3) = 42
    c: Symmetric(g0,g4,g-2)
    c: DistanceX(g5,g5) = 15
    c: Symmetric(g1,g3,g6)
    c: Coincident(g7,g6)
    c: Diameter(g7) = 22.5
    c: DistanceY(g-1,g3) = 11
FEATURE [PartDesign::Pad] Pad006
  BaseFeature = -> Pad005
  Direction = (1,0,0)
  Length = 4
  Length2 = 10
  Profile = -> Sketch011
  ReferenceAxis = -> Sketch011 [N_Axis]
  Refine = true
  Reversed = true
  Type = 0
FEATURE [Sketcher::SketchObject] Sketch012
  ExternalGeometry = -> [Pad006]
  FullyConstrained = true
  MapMode = 5
  Placement = pos=(11,0,0) rot=(0.57735,-0.57735,-0.57735;2.0944rad)
  Support = -> [Pad006]
  sketch-geometry (5):
    g0: Circle CenterX=15.5 CenterY=47.5 CenterZ=0 NormalX=0 NormalY=0 NormalZ=1 AngleXU=0 Radius=1.5
    g1: LineSegment StartX=1.2e-15 StartY=32 StartZ=0 EndX=11.25 EndY=32 EndZ=0
    g2: Circle CenterX=-15.5 CenterY=47.5 CenterZ=0 NormalX=0 NormalY=0 NormalZ=1 AngleXU=0 Radius=1.5
    g3: Circle CenterX=15.5 CenterY=16.5 CenterZ=0 NormalX=0 NormalY=0 NormalZ=1 AngleXU=0 Radius=1.5
    g4: Circle CenterX=-15.5 CenterY=16.5 CenterZ=0 NormalX=0 NormalY=0 NormalZ=1 AngleXU=0 Radius=1.5
  constraints (12):
    c: DistanceY(g-3,g0) = 15.5
    c: DistanceX(g-3,g0) = 15.5
    c: Diameter(g0) = 3
    c: Coincident(g1,g-3)
    c: Horizontal(g1)
    c: PointOnObject(g1,g-3)
    c: Diameter(g2) = 3
    c: Diameter(g3) = 3
    c: Diameter(g4) = 3
    c: Symmetric(g2,g0,g-2)
    c: Symmetric(g4,g3,g-2)
    c: Symmetric(g3,g0,g1)
FEATURE [PartDesign::Hole] Hole002
  BaseFeature = -> Pad006
  CustomThreadClearance = 0
  Depth = 25
  DepthType = 0
  Diameter = 3.4
  DrillForDepth = false
  DrillPoint = 1
  DrillPointAngle = 118
  HoleCutCountersinkAngle = 90
  HoleCutCustomValues = false
  HoleCutDepth = 2
  HoleCutDiameter = 6.1
  HoleCutType = 1
  ModelThread = false
  Profile = -> Sketch012
  Refine = true
  Tapered = false
  TaperedAngle = 90
  ThreadClass = 0
  ThreadDepth = 25
  ThreadDepthType = 0
  ThreadDirection = 0
  ThreadFit = 0
  ThreadSize = 9
  ThreadType = 1
  Threaded = false
  UseCustomThreadClearance = false
FEATURE [Sketcher::SketchObject] Sketch013
  ExternalGeometry = -> [Hole002]
  FullyConstrained = true
  MapMode = 5
  Placement = pos=(0,0,20) rot=(0,0,1;0rad)
  Support = -> [Hole002]
  sketch-geometry (1):
    g0: Circle CenterX=0 CenterY=0 CenterZ=0 NormalX=0 NormalY=0 NormalZ=1 AngleXU=0 Radius=2.5
  constraints (2):
    c: Coincident(g0,g-3)
    c: Equal(g0,g-3)
FEATURE [PartDesign::Pad] Pad007
  BaseFeature = -> Hole002
  Direction = (0,0,1)
  Length = 2
  Length2 = 10
  Profile = -> Sketch013
  ReferenceAxis = -> Sketch013 [N_Axis]
  Refine = true
  Reversed = true
  Type = 0
FEATURE [Sketcher::SketchObject] Sketch017
  ExternalGeometry = -> [Pad007]
  FullyConstrained = true
  MapMode = 5
  Placement = pos=(0,0,0) rot=(1,0,0;3.14159rad)
  sketch-geometry (5):
    g0: Circle CenterX=-150 CenterY=4.1e-15 CenterZ=0 NormalX=0 NormalY=0 NormalZ=1 AngleXU=0 Radius=8
    g1: ArcOfCircle CenterX=-150 CenterY=4.1e-15 CenterZ=0 NormalX=0 NormalY=0 NormalZ=1 AngleXU=0 Radius=11 StartAngle=0.276227 EndAngle=6.00696
    g2: ArcOfCircle CenterX=7.9e-15 CenterY=2e-14 CenterZ=0 NormalX=0 NormalY=0 NormalZ=1 AngleXU=0 Radius=7.5 StartAngle=2.73008 EndAngle=3.55311
    g3: LineSegment StartX=-139.417 StartY=3 StartZ=0 EndX=-6.87386 EndY=3 EndZ=0
    g4: LineSegment StartX=-139.417 StartY=-3 StartZ=0 EndX=-6.87386 EndY=-3 EndZ=0
  constraints (15):
    c: Coincident(g1,g0)
    c: Horizontal(g3)
    c: Horizontal(g4)
    c: Coincident(g1,g4)
    c: Coincident(g1,g3)
    c: Coincident(g2,g3)
    c: Coincident(g2,g4)
    c: Symmetric(g1,g1,g-1)
    c: Distance(g1,g1) = 6
    c: Diameter(g0) = 16
    c: Diameter(g1) = 22
    c: DistanceX(g0,g-1) = 150
    c: Equal(g2,g-3)
    c: PointOnObject(g2,g-3)
    c: Equal(g4,g3)
FEATURE [PartDesign::Pad] Pad008
  BaseFeature = -> Pad007
  Direction = (0,0,-1)
  Length = 10
  Length2 = 10
  Profile = -> Sketch017
  ReferenceAxis = -> Sketch017 [N_Axis]
  Refine = true
  Reversed = true
  Type = 0
FEATURE [PartDesign::Plane] DatumPlane001
  AttachmentOffset = pos=(0,0,-145) rot=(0,0,1;0rad)
  Length = 62.49
  MapMode = 5
  Placement = pos=(-130,0,0) rot=(0.57735,0.57735,0.57735;2.0944rad)
  ResizeMode = 0
  Support = -> [Pad008]
  Width = 90.49
FEATURE [Sketcher::SketchObject] Sketch018
  ExternalGeometry = -> [Pad008]
  FullyConstrained = true
  MapMode = 5
  Placement = pos=(-130,0,0) rot=(0.57735,0.57735,0.57735;2.0944rad)
  Support = -> [DatumPlane001]
  sketch-geometry (5):
    g0: Circle CenterX=-1.2e-15 CenterY=32 CenterZ=0 NormalX=0 NormalY=0 NormalZ=1 AngleXU=0 Radius=8
    g1: ArcOfCircle CenterX=-1.2e-15 CenterY=32 CenterZ=0 NormalX=0 NormalY=0 NormalZ=1 AngleXU=0 Radius=11 StartAngle=4.98862 EndAngle=10.7193
    g2: LineSegment StartX=-3 StartY=10 StartZ=0 EndX=-3 EndY=21.417 EndZ=0
    g3: LineSegment StartX=3 StartY=10 StartZ=0 EndX=3 EndY=21.417 EndZ=0
    g4: LineSegment StartX=-3 StartY=10 StartZ=0 EndX=3 EndY=10 EndZ=0
  constraints (12):
    c: Coincident(g0,g-3)
    c: Coincident(g1,g0)
    c: Diameter(g0) = 16
    c: Diameter(g1) = 22
    c: Vertical(g3)
    c: Vertical(g2)
    c: Coincident(g1,g2)
    c: Coincident(g1,g3)
    c: Symmetric(g2,g3,g-2)
    c: Coincident(g4,g2)
    c: Coincident(g4,g3)
    c: Coincident(g2,g-4)
FEATURE [PartDesign::Pad] Pad009
  BaseFeature = -> Pad008
  Direction = (1,0,0)
  Length = 5
  Length2 = 10
  Profile = -> Sketch018
  ReferenceAxis = -> Sketch018 [N_Axis]
  Refine = true
  Type = 0
FEATURE [PartDesign::Body] Body001  label="arm1-skel"
  Group = -> [Sketch010,Pad005,Sketch011,Pad006,Sketch012,Hole002,Sketch013,Pad007,Sketch017,Pad008,DatumPlane001,Sketch018,Pad009]
  Origin = -> Origin002
  Tip = -> Pad009
FEATURE [PartDesign::Chamfer] Chamfer
  Angle = 15
  Base = -> Pad004
  BaseFeature = -> Pad004
  ChamferType = 2
  FlipDirection = true
  Refine = true
  Size = 1
  Size2 = 1
  SupportTransform = false
  UseAllEdges = false
FEATURE [PartDesign::Chamfer] Chamfer001
  Angle = 15
  Base = -> Chamfer [Edge18]
  BaseFeature = -> Chamfer
  ChamferType = 2
  FlipDirection = true
  Refine = true
  Size = 5
  Size2 = 1
  SupportTransform = false
  UseAllEdges = false
FEATURE [PartDesign::Chamfer] Chamfer002
  Angle = 15
  Base = -> Chamfer001 [Edge99]
  BaseFeature = -> Chamfer001
  ChamferType = 2
  FlipDirection = false
  Refine = true
  Size = 1
  Size2 = 1
  SupportTransform = false
  UseAllEdges = false
FEATURE [PartDesign::Chamfer] Chamfer003
  Angle = 15
  Base = -> Chamfer002 [Edge39]
  BaseFeature = -> Chamfer002
  ChamferType = 2
  FlipDirection = true
  Refine = true
  Size = 3
  Size2 = 1
  SupportTransform = false
  UseAllEdges = false
FEATURE [PartDesign::Chamfer] Chamfer004
  Angle = 15
  Base = -> Chamfer003 [Edge79]
  BaseFeature = -> Chamfer003
  ChamferType = 2
  FlipDirection = false
  Refine = true
  Size = 1
  Size2 = 1
  SupportTransform = false
  UseAllEdges = false
FEATURE [PartDesign::Chamfer] Chamfer005
  Angle = 15
  Base = -> Chamfer004 [Edge35,Edge87]
  BaseFeature = -> Chamfer004
  ChamferType = 2
  FlipDirection = true
  Refine = true
  Size = 1
  Size2 = 1
  SupportTransform = false
  UseAllEdges = false
FEATURE [PartDesign::Chamfer] Chamfer006
  Angle = 45
  Base = -> Chamfer005 [Edge5,Edge29]
  BaseFeature = -> Chamfer005
  ChamferType = 0
  FlipDirection = false
  Refine = true
  Size = 7
  Size2 = 1
  SupportTransform = false
  UseAllEdges = false
FEATURE [PartDesign::Plane] DatumPlane002
  Length = 62.49
  MapMode = 5
  Placement = pos=(-125,0,0) rot=(0.57735,0.57735,0.57735;2.0944rad)
  ResizeMode = 0
  Support = -> [Chamfer006]
  Width = 90.49
FEATURE [Sketcher::SketchObject] Sketch019
  ExternalGeometry = -> [Chamfer006]
  FullyConstrained = true
  MapMode = 5
  Placement = pos=(-125,0,0) rot=(0.57735,0.57735,0.57735;2.0944rad)
  Support = -> [DatumPlane002]
  sketch-geometry (4):
    g0: ArcOfCircle CenterX=-1.2e-15 CenterY=32 CenterZ=0 NormalX=0 NormalY=0 NormalZ=1 AngleXU=0 Radius=11 StartAngle=3.39743 EndAngle=6.02735
    g1: LineSegment StartX=-10.642 StartY=29.2164 StartZ=0 EndX=-3 EndY=0 EndZ=0
    g2: LineSegment StartX=-3 StartY=0 StartZ=0 EndX=3 EndY=0 EndZ=0
    g3: LineSegment StartX=3 StartY=0 StartZ=0 EndX=10.642 EndY=29.2164 EndZ=0
  constraints (9):
    c: Coincident(g0,g-3)
    c: PointOnObject(g-3,g0)
    c: PointOnObject(g1,g-1)
    c: Coincident(g1,g2)
    c: Coincident(g2,g3)
    c: Tangent(g0,g1) = -1.5708
    c: Tangent(g0,g3) = -1.5708
    c: Distance(g2,g2) = 6
    c: Symmetric(g1,g2,g-2)
FEATURE [PartDesign::Pad] Pad010
  BaseFeature = -> Chamfer006
  Direction = (1,0,0)
  Length = 10
  Length2 = 10
  Profile = -> Sketch019
  ReferenceAxis = -> Sketch019 [N_Axis]
  Refine = true
  Reversed = true
  Type = 3
  UpToFace = -> Chamfer006 [Face1]
FEATURE [PartDesign::Plane] DatumPlane003
  Length = 62.49
  MapMode = 5
  Placement = pos=(15,0,0) rot=(0.57735,0.57735,0.57735;2.0944rad)
  ResizeMode = 0
  Support = -> [Pad010]
  Width = 90.49
FEATURE [Sketcher::SketchObject] Sketch020
  ExternalGeometry = -> [Pad010]
  FullyConstrained = true
  MapMode = 5
  Placement = pos=(15,0,0) rot=(0.57735,0.57735,0.57735;2.0944rad)
  Support = -> [DatumPlane003]
  sketch-geometry (4):
    g0: ArcOfCircle CenterX=0 CenterY=47 CenterZ=0 NormalX=0 NormalY=0 NormalZ=1 AngleXU=0 Radius=2 StartAngle=0.664501 EndAngle=2.47709
    g1: ArcOfCircle CenterX=-1.2e-15 CenterY=32 CenterZ=0 NormalX=0 NormalY=0 NormalZ=1 AngleXU=0 Radius=11.25 StartAngle=0.664501 EndAngle=2.47709
    g2: LineSegment StartX=-8.85627 StartY=38.9375 StartZ=0 EndX=-1.57445 EndY=48.2333 EndZ=0
    g3: LineSegment StartX=8.85627 StartY=38.9375 StartZ=0 EndX=1.57445 EndY=48.2333 EndZ=0
  constraints (11):
    c: PointOnObject(g0,g-2)
    c: Coincident(g1,g-3)
    c: PointOnObject(g1,g-3)
    c: Horizontal(g1,g1)
    c: Tangent(g2,g1) = 1.5708
    c: Coincident(g3,g1)
    c: Equal(g3,g2)
    c: Coincident(g0,g2)
    c: Tangent(g0,g3) = -1.5708
    c: DistanceY(g1,g0) = 15
    c: Radius(g0) = 2
FEATURE [PartDesign::Pocket] Pocket002
  BaseFeature = -> Pad010
  Direction = (-1,0,0)
  Length = 5
  Length2 = 5
  Profile = -> Sketch020
  ReferenceAxis = -> Sketch020 [N_Axis]
  Refine = true
  Type = 0
FEATURE [PartDesign::Chamfer] Chamfer007
  Angle = 45
  Base = -> Pocket002 [Edge18,Edge6]
  BaseFeature = -> Pocket002
  ChamferType = 0
  FlipDirection = false
  Refine = true
  Size = 2
  Size2 = 1
  SupportTransform = false
  UseAllEdges = false
FEATURE [PartDesign::Fillet] Fillet
  Base = -> Chamfer007 [Edge65,Edge142,Edge84,Edge143]
  BaseFeature = -> Chamfer007
  Radius = 6
  Refine = true
  SupportTransform = false
  UseAllEdges = false
FEATURE [PartDesign::Body] Body  label="arm1s"
  Group = -> [Sketch,Pad,Sketch001,Pad001,Sketch003,Hole,Sketch004,Pad002,Sketch005,Pocket,Sketch006,Hole001,Sketch007,Pocket001,Sketch008,Pad003,DatumPlane,Sketch009,Pad004,Chamfer,Chamfer001,Chamfer002,Chamfer003,Chamfer004,Chamfer005,Chamfer006,DatumPlane002,Sketch019,Pad010,DatumPlane003,Sketch020,Pocket002,Chamfer007,Fillet]
  Origin = -> Origin001
  Tip = -> Fillet
FEATURE [App::Part] Part  label="arm1"
  Group = -> [Body001,Body]
  Origin = -> Origin
---- part arm2.FCStd = doc fcstd_0a79d40cf136 ----
FCSTD DOCUMENT  (FreeCAD 2024.1R35694 (Git))
Label: arm2
License: All rights reserved
LicenseURL: https://en.wikipedia.org/wiki/All_rights_reserved
objects: Sketcher::SketchObject×3, PartDesign::Pad×2, PartDesign::Body×2, PartDesign::Chamfer×1, PartDesign::Pocket×1, App::Part×1
note: 13 computed .brp shape members not serialized (recipe doc carries the construction recipe); baked Part::Feature solids carry a one-line shape summary decoded from their .brp

FEATURE [Sketcher::SketchObject] Sketch
  FullyConstrained = true
  MapMode = 5
  Support = -> [XY_Plane001]
  sketch-geometry (9):
    g0: ArcOfCircle CenterX=0 CenterY=0 CenterZ=0 NormalX=0 NormalY=0 NormalZ=1 AngleXU=0 Radius=2.5 StartAngle=2.2143 EndAngle=4.06889
    g1: ArcOfCircle CenterX=0 CenterY=0 CenterZ=0 NormalX=0 NormalY=0 NormalZ=1 AngleXU=0 Radius=4 StartAngle=0.523599 EndAngle=5.75959
    g2: LineSegment StartX=3.4641 StartY=2 StartZ=0 EndX=118 EndY=2 EndZ=0
    g3: LineSegment StartX=118 StartY=2 StartZ=0 EndX=120 EndY=0 EndZ=0
    g4: LineSegment StartX=120 StartY=0 StartZ=0 EndX=118 EndY=-2 EndZ=0
    g5: LineSegment StartX=118 StartY=-2 StartZ=0 EndX=3.4641 EndY=-2 EndZ=0
    g6: LineSegment StartX=-1.5 StartY=2 StartZ=0 EndX=1.5 EndY=2 EndZ=0
    g7: LineSegment StartX=-1.5 StartY=-2 StartZ=0 EndX=1.5 EndY=-2 EndZ=0
    g8: ArcOfCircle CenterX=0 CenterY=0 CenterZ=0 NormalX=0 NormalY=0 NormalZ=1 AngleXU=0 Radius=2.5 StartAngle=5.35589 EndAngle=7.21048
  constraints (26):
    c: Coincident(g0,g-1)
    c: Coincident(g1,g0)
    c: Horizontal(g2)
    c: Coincident(g2,g3)
    c: PointOnObject(g3,g-1)
    c: Coincident(g3,g4)
    c: Coincident(g4,g5)
    c: Horizontal(g6)
    c: Horizontal(g7)
    c: Equal(g6,g7)
    c: Coincident(g0,g6)
    c: Equal(g0,g8)
    c: Coincident(g0,g7)
    c: Coincident(g8,g7)
    c: Coincident(g0,g8)
    c: Diameter(g8) = 5
    c: DistanceY(g7,g6) = 4
    c: Symmetric(g4,g2,g-1)
    c: Angle(g3,g4) = 1.5708
    c: Distance(g2,g4) = 4
    c: Coincident(g1,g5)
    c: Diameter(g1) = 8
    c: DistanceX(g-1,g3) = 120
    c: Coincident(g1,g2)
    c: Equal(g5,g2)
    c: Coincident(g6,g8)
FEATURE [PartDesign::Pad] Pad
  Direction = (0,0,1)
  Length = 5
  Length2 = 10
  Profile = -> Sketch
  ReferenceAxis = -> Sketch [N_Axis]
  Refine = true
  Type = 0
FEATURE [PartDesign::Body] Body  label="arm2-skel"
  Group = -> [Sketch,Pad]
  Origin = -> Origin001
  Tip = -> Pad
FEATURE [Sketcher::SketchObject] Sketch001
  FullyConstrained = true
  MapMode = 5
  Support = -> [XY_Plane002]
  sketch-geometry (9):
    g0: ArcOfCircle CenterX=0 CenterY=0 CenterZ=0 NormalX=0 NormalY=0 NormalZ=1 AngleXU=0 Radius=2.5 StartAngle=2.2143 EndAngle=4.06889
    g1: ArcOfCircle CenterX=0 CenterY=0 CenterZ=0 NormalX=0 NormalY=0 NormalZ=1 AngleXU=0 Radius=4 StartAngle=0.523599 EndAngle=5.75959
    g2: LineSegment StartX=3.4641 StartY=2 StartZ=0 EndX=118 EndY=2 EndZ=0
    g3: LineSegment StartX=118 StartY=2 StartZ=0 EndX=120 EndY=0 EndZ=0
    g4: LineSegment StartX=120 StartY=0 StartZ=0 EndX=118 EndY=-2 EndZ=0
    g5: LineSegment StartX=118 StartY=-2 StartZ=0 EndX=3.4641 EndY=-2 EndZ=0
    g6: LineSegment StartX=-1.5 StartY=2 StartZ=0 EndX=1.5 EndY=2 EndZ=0
    g7: LineSegment StartX=-1.5 StartY=-2 StartZ=0 EndX=1.5 EndY=-2 EndZ=0
    g8: ArcOfCircle CenterX=0 CenterY=0 CenterZ=0 NormalX=0 NormalY=0 NormalZ=1 AngleXU=0 Radius=2.5 StartAngle=5.35589 EndAngle=7.21048
  constraints (26):
    c: Coincident(g0,g-1)
    c: Coincident(g1,g0)
    c: Horizontal(g2)
    c: Coincident(g2,g3)
    c: PointOnObject(g3,g-1)
    c: Coincident(g3,g4)
    c: Coincident(g4,g5)
    c: Horizontal(g6)
    c: Horizontal(g7)
    c: Equal(g6,g7)
    c: Coincident(g0,g6)
    c: Equal(g0,g8)
    c: Coincident(g0,g7)
    c: Coincident(g8,g7)
    c: Coincident(g0,g8)
    c: Diameter(g8) = 5
    c: DistanceY(g7,g6) = 4
    c: Symmetric(g4,g2,g-1)
    c: Angle(g3,g4) = 1.5708
    c: Distance(g2,g4) = 4
    c: Coincident(g1,g5)
    c: Diameter(g1) = 8
    c: DistanceX(g-1,g3) = 120
    c: Coincident(g1,g2)
    c: Equal(g5,g2)
    c: Coincident(g6,g8)
FEATURE [PartDesign::Pad] Pad001
  Direction = (0,0,1)
  Length = 5
  Length2 = 10
  Profile = -> Sketch001
  ReferenceAxis = -> Sketch001 [N_Axis]
  Refine = true
  Type = 0
FEATURE [PartDesign::Chamfer] Chamfer
  Angle = 15
  Base = -> Pad001 [Edge24,Edge21,Edge18,Edge26,Edge25,Edge27,Edge19,Edge22]
  BaseFeature = -> Pad001
  ChamferType = 2
  FlipDirection = false
  Refine = true
  Size = 1
  Size2 = 1
  SupportTransform = false
  UseAllEdges = false
FEATURE [Sketcher::SketchObject] Sketch002
  ExternalGeometry = -> [Chamfer]
  FullyConstrained = true
  MapMode = 5
  Placement = pos=(0,0,5) rot=(0,0,1;0rad)
  Support = -> [Chamfer]
  sketch-geometry (4):
    g0: LineSegment StartX=3.4641 StartY=-2 StartZ=0 EndX=203.464 EndY=-2 EndZ=0
    g1: LineSegment StartX=203.464 StartY=-2 StartZ=0 EndX=203.464 EndY=2 EndZ=0
    g2: LineSegment StartX=203.464 StartY=2 StartZ=0 EndX=3.4641 EndY=2 EndZ=0
    g3: ArcOfCircle CenterX=0 CenterY=0 CenterZ=0 NormalX=0 NormalY=0 NormalZ=1 AngleXU=0 Radius=4 StartAngle=5.75959 EndAngle=6.80678
  constraints (11):
    c: Coincident(g0,g1)
    c: Coincident(g1,g2)
    c: Vertical(g1)
    c: Horizontal(g0)
    c: Horizontal(g2)
    c: Coincident(g3,g-3)
    c: Coincident(g2,g-3)
    c: Coincident(g0,g-3)
    c: DistanceX(g2,g2) = 200
    c: Coincident(g3,g2)
    c: PointOnObject(g3,g0)
FEATURE [PartDesign::Pocket] Pocket
  BaseFeature = -> Chamfer
  Direction = (0,0,-1)
  Length = 1
  Length2 = 5
  Profile = -> Sketch002
  ReferenceAxis = -> Sketch002 [N_Axis]
  Refine = true
  Type = 0
FEATURE [PartDesign::Body] Body001  label="arm2s"
  Group = -> [Sketch001,Pad001,Chamfer,Sketch002,Pocket]
  Origin = -> Origin002
  Tip = -> Pocket
FEATURE [App::Part] Part  label="arm2"
  Group = -> [Body,Body001]
  Origin = -> Origin
